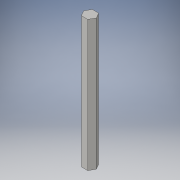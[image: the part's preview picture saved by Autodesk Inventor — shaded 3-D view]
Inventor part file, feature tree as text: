
AUTODESK INVENTOR PART (.ipt)
format: ipt  version: 2016 (Build 200138000, 138)  size: 90,112 bytes
history: native  units: in
note: dims shown in document units (in); Inventor stores cm internally (conversion verified against a paired STEP export)
features: extrude x1, sketch x1
ambient origin geometry x8: Origin, YZ Plane, XZ Plane, XY Plane, X Axis, Y Axis, Z Axis, Center Point
bodies: Solid1 (feature_tree)
feature tree (2):
  extrude  "Extrusion1"  Depth=6.0in TaperAngle=0.0deg
  sketch  "Sketch1"  dims[d0=0.5in d1=6.0in d2=0.0in]
